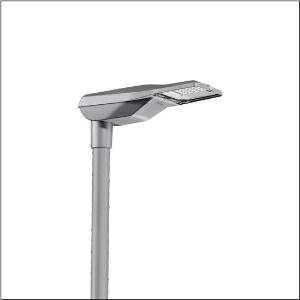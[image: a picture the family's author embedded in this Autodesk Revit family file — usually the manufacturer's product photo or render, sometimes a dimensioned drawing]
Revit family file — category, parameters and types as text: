
# Revit family: streetlight_sl_21_micro___stw1_0a_5xe5e43a08cb_47df
name_source: partatom
category: Lighting Fixtures
units: mm (PartAtom-declared; Revit-internal decimal feet)

## family parameters
Cut with Voids When Loaded = No
Host = Face
Light Source = No
Part Type = Normal
Room Calculation Point = No
Round Connector Dimension = Use Diameter
Shared = No

## types (1)
- --- (1 x LED, 2380 lm, 15.8 W, 4000K)
    Apparent Load = 16 VA
    CIE Flux Codes = 38 75 98 100 100
    Color Rendering = 70
    Color Temperature = 4000K
    Default Elevation = 1800 mm
    Description = Streetlight SL 21 micro, mast luminaire, primary light control with lens, of PMMA, primary optical cover: cover, of toughened safety glass, transparent, light distribution: STW1.0a, light emission: direct distribution, primary light characteristic: asymmetric, installation type: side-entry, post-top, LED, 3G 1.5mm², High Power LED, rated luminous flux: 2.380lm, luminous efficacy: 151lm/W, light colour: 740, colour temperature: 4000K, control: flexible luminous flux parameterisation, time-dependent luminous flux control, constant luminous flux control, overheat protection, mains connection: 230..240V, AC, 50/60Hz, connection cable pre-assembled, cable length: 5,5m, wiring characteristics: H07RN-F, start of lifetime: 16W, end of service life: 16W, reduction: 9W, luminaire housing, of diecast aluminium, powder-coated, Siteco® metallic grey (DB 702S), corrosivity category C5 mid according to DIN EN ISO 12944, please order mast flange separately, inclination adjustable: 0°, 5°, 10°, 15°, sealing non-destructively replaceable, multi-level sealing system, length: 528mm, width: 235mm, height: 110mm, mast flange for spigot size: 42mm (side-entry): 5XC10008XM4, 60/48mm (side-entry/post-top): 5XC10108XM2, 76/60mm (side-entry/post-top): 5XC10108XM1, protection rating (complete): IP66, insulation class (complete): insulation class II (safety insulation), certification: CE, ENEC, ENEC+, VDE, impact resistance: IK09, permissible operating ambient temperature for outdoor applications: -40..+50°C, standard-compliant lighting for roads and squares, packaging unit: 1 piece

Light Distribution: STW1.0a
    Height = 110 mm
    Lamp = 1 x LED
    Lamp Light Flux = 2380 lm
    Lamp Power = 15.8 W
    Lamp count = 1
    Length = 528 mm
    Luminous efficacy = 151 lm/W
    Manufacturer = Siteco
    ModVariant = No
    Model = 5XE5E43A08CB
    Number of Poles = 1
    OnlyDefault = Yes
    Power Factor = 1
    Product Name = Streetlight SL 21 micro | STW1.0a
    Product group = mast luminaire | pylon top
    ProductGroupID = 6100
    Protection Class = Protection class II
    Protection Degree = IP 66
    RLX_Detail_Level = 1
    RLX_Emergency_Light_Flux = 0 lm
    RLX_Emergency_Type = 0
    RLX_Emergency_Type_DB = No
    RlxData = <blob elided: 97609 chars, md5=13a98f12>
    Socket = socket
    Standby Power = 0 W
    System Light Flux = 2380 lm
    System Power = 16 W
    Type Comments = factory setting: luminous flux: 100 % | Output Level: 100 % | 300 mA
    Type Image = l_1006881.jpg
    URL = http://relux.com
    VarID = @adj_087417
    Voltage = 0 V
    Weight = 0.00 kg
    Width = 235 mm

## geometry (parser evidence)
native form markers: Blend x4, Sweep x10
no freeform markers — native parametric forms only
